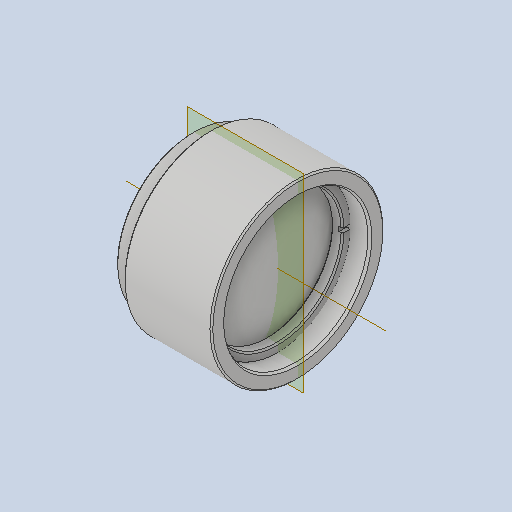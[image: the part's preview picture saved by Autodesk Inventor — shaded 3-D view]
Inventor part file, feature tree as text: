
AUTODESK INVENTOR PART (.ipt)
format: ipt  version: 2023 (Build 270158000, 158)  size: 441,856 bytes
history: native  units: mm
features: other x9, plane x2
ambient origin geometry x8: Origin, YZ Plane, XZ Plane, XY Plane, X Axis, Y Axis, Z Axis, Center Point
bodies: Solid1 (feature_tree), Solid2 (feature_tree), Solid3 (feature_tree), Solid4 (feature_tree)
feature tree (11):
  plane  "Work Plane2"
  other  "Work Axis1"
  other  "Work Point1"
  plane  "Work Plane1"
  other  "20619-001-1-solid1"
  other  "20526-001-1-solid1"
  other  "20526-001-1-solid2"
  other  "0082-001-1-solid1"
  other  "<userpath> Lab\Documents\UC2-INVENTOR-Git\uc2_v3\Assembly_Cube_Thorlabs_Cage_v3.iam"
  other  "Assembly_Cube_Thorlabs_Cage_v3.iam"
  other  "20_Cube_Insert_Thorlabs_SM1Tube:1"
